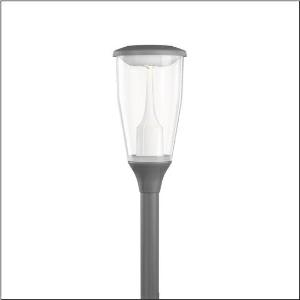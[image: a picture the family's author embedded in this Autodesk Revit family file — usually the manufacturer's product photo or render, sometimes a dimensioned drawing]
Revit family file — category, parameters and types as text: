
# Revit family: dl_11_iq___p1_0a_5xa5565nf14h000022_7674
name_source: partatom
category: Lighting Fixtures
units: mm (PartAtom-declared; Revit-internal decimal feet)

## family parameters
Cut with Voids When Loaded = No
Host = Face
Light Source = No
Part Type = Normal
Room Calculation Point = No
Round Connector Dimension = Use Diameter
Shared = No

## types (1)
- --- (1 x LED, 1530 lm, 11.8 W, 2700K)
    Apparent Load = 12 VA
    CIE Flux Codes = 34 63 91 95 100
    Color Rendering = 70
    Color Temperature = 2700K
    Default Elevation = 1800 mm
    Description = DL 11 iQ, mast luminaire, Module 540 iQ-SR, primary light control with 3 zone facetted reflector, of plastic, silver coated, highly specular, structured, primary optical cover: cover, of PMMA, transparent, light distribution: P1.0a, light emission: direct distribution, primary light characteristic: asymmetric, installation type: post-top, LED, High Power LED, rated luminous flux: 1.560lm, luminous efficacy: 149lm/W, light colour: 727, colour temperature: 2700K, control: Street-Remote, Auto-Match, Temp-Guard, Lumen-Switch, Night-Set, Smart-Wire, Light-Fading, Desk-Remote (wireless, voltage-free reading and setting of iQ features in the workshop via application-optimized NFC function/RFID function), optimised constant luminous flux control (CLO 2.0), mains connection: 220..240V, AC, 50/60Hz, connection cable pre-assembled, cable length: 5,5m, start of lifetime: 12W, end of service life: 12W, reduction: 5W, luminaire housing, upper part, of diecast aluminium, coated, Siteco® metallic grey (DB 702S), spigot size: 60mm (post-top), post-top mast mounting element, of diecast aluminium, coated, Siteco® metallic grey (DB 702S), Module 540 iQ-SR, traffic white (RAL 9016), equipment: standard, protection rating (complete): IP66, insulation class (complete): insulation class II (safety insulation), certification: CE, ENEC, ENEC+, VDE, packaging unit: 1 piece

Light Distribution: P1.0a
    Height = 665 mm
    Lamp = 1 x LED
    Lamp Light Flux = 1530 lm
    Lamp Power = 11.8 W
    Lamp count = 1
    Length = 334 mm
    Luminous efficacy = 130 lm/W
    Manufacturer = Siteco
    ModVariant = No
    Model = 5XA5565NF14H000022
    Number of Poles = 1
    OnlyDefault = Yes
    Power Factor = 1
    Product Name = DL 11 iQ | P1.0a
    Product group = mast luminaire | pylon top
    ProductGroupID = 6100
    Protection Class = Protection class II
    Protection Degree = IP 66
    RLX_Detail_Level = 1
    RLX_Emergency_Light_Flux = 0 lm
    RLX_Emergency_Type = 0
    RLX_Emergency_Type_DB = No
    RlxData = <blob elided: 103633 chars, md5=1daa49f3>
    Socket = socket
    Standby Power = 0 W
    System Light Flux = 1530 lm
    System Power = 12 W
    Type Comments = factory setting: luminous flux: 100 % | dim-lin: 254 | 472 mA
    Type Image = l_1258354.jpg
    URL = http://relux.com
    VarID = @adj_024215
    Voltage = 0 V
    Weight = 0.00 kg
    Width = 0 mm  [stored 0 ft]

note: [stored X ft] marks values corroborated as IEEE doubles in the binary element streams (Revit-internal decimal feet)

## geometry (parser evidence)
native form markers: Blend x4, Sweep x10
no freeform markers — native parametric forms only
